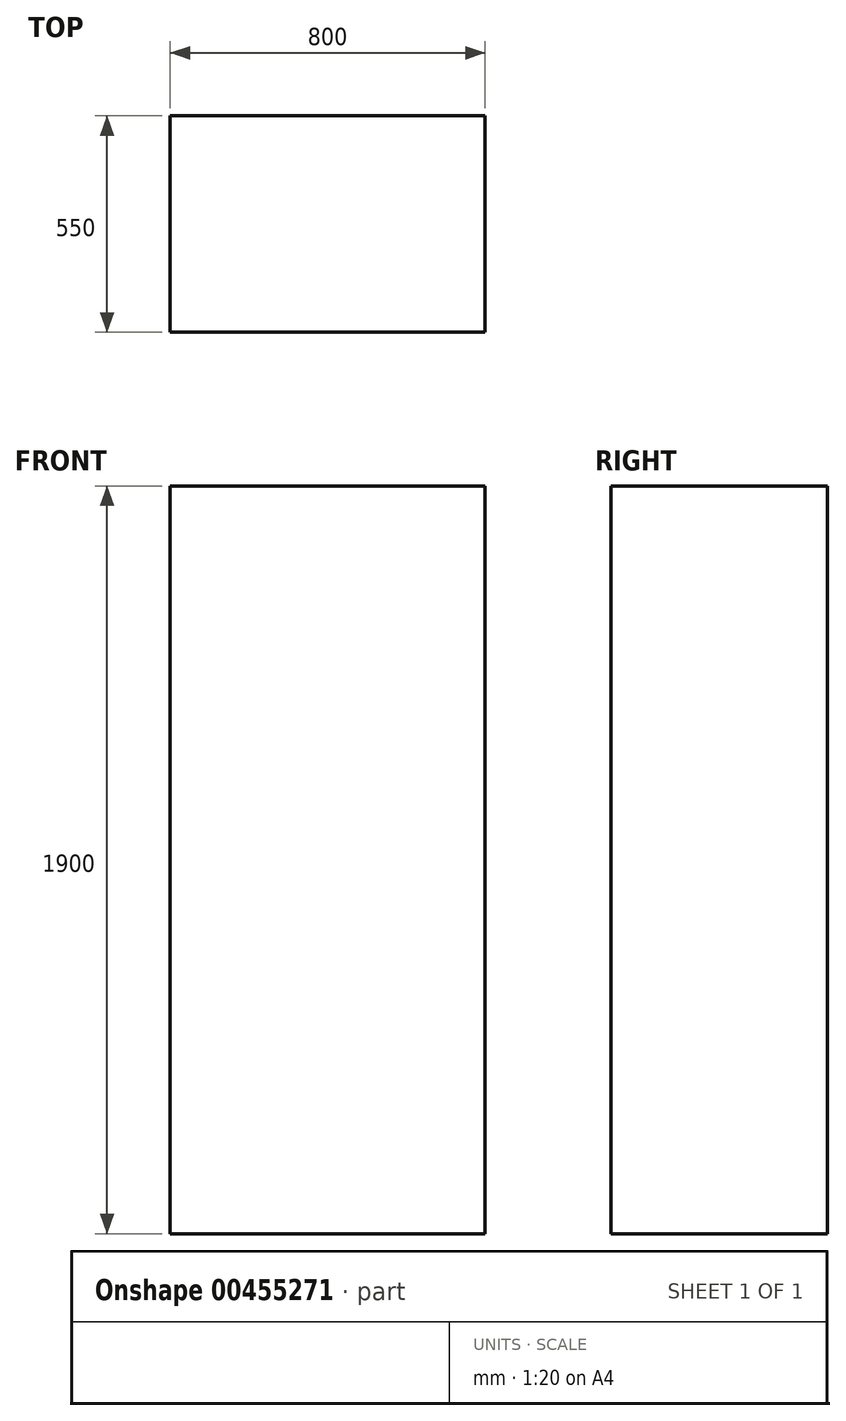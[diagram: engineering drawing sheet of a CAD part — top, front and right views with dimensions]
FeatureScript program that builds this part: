
annotation { "Feature Type Name" : "Feature", "Feature Type Description" : "" }
export const myFeature = defineFeature(function(context is Context, id is Id, definition is map)
    precondition{}
    {
        {
            var Q0;
            Q0=qCreatedBy(makeId("Top.planeOp"),FACE);
            var sketch = newSketch(context, id + "F0", { "sketchPlane" : qUnion([Q0])});
            skLineSegment(sketch, "E0.bottom", {"start": v(-58.82, 507.43) * mm, "end": v(741.18, 507.43) * mm});
            skLineSegment(sketch, "E0.top", {"start": v(-58.82, -42.57) * mm, "end": v(741.18, -42.57) * mm});
            skLineSegment(sketch, "E0.left", {"start": v(-58.82, 507.43) * mm, "end": v(-58.82, -42.57) * mm});
            skLineSegment(sketch, "E0.right", {"start": v(741.18, 507.43) * mm, "end": v(741.18, -42.57) * mm});
            skSolve(sketch);
        }
        {
            var Q0;
            Q0=qSketchRegion(id+"F0",true);
            extrude(context, id + "F1", {"entities" : qUnion([Q0]), "depth" : 1900 * mm});
        }
    });
